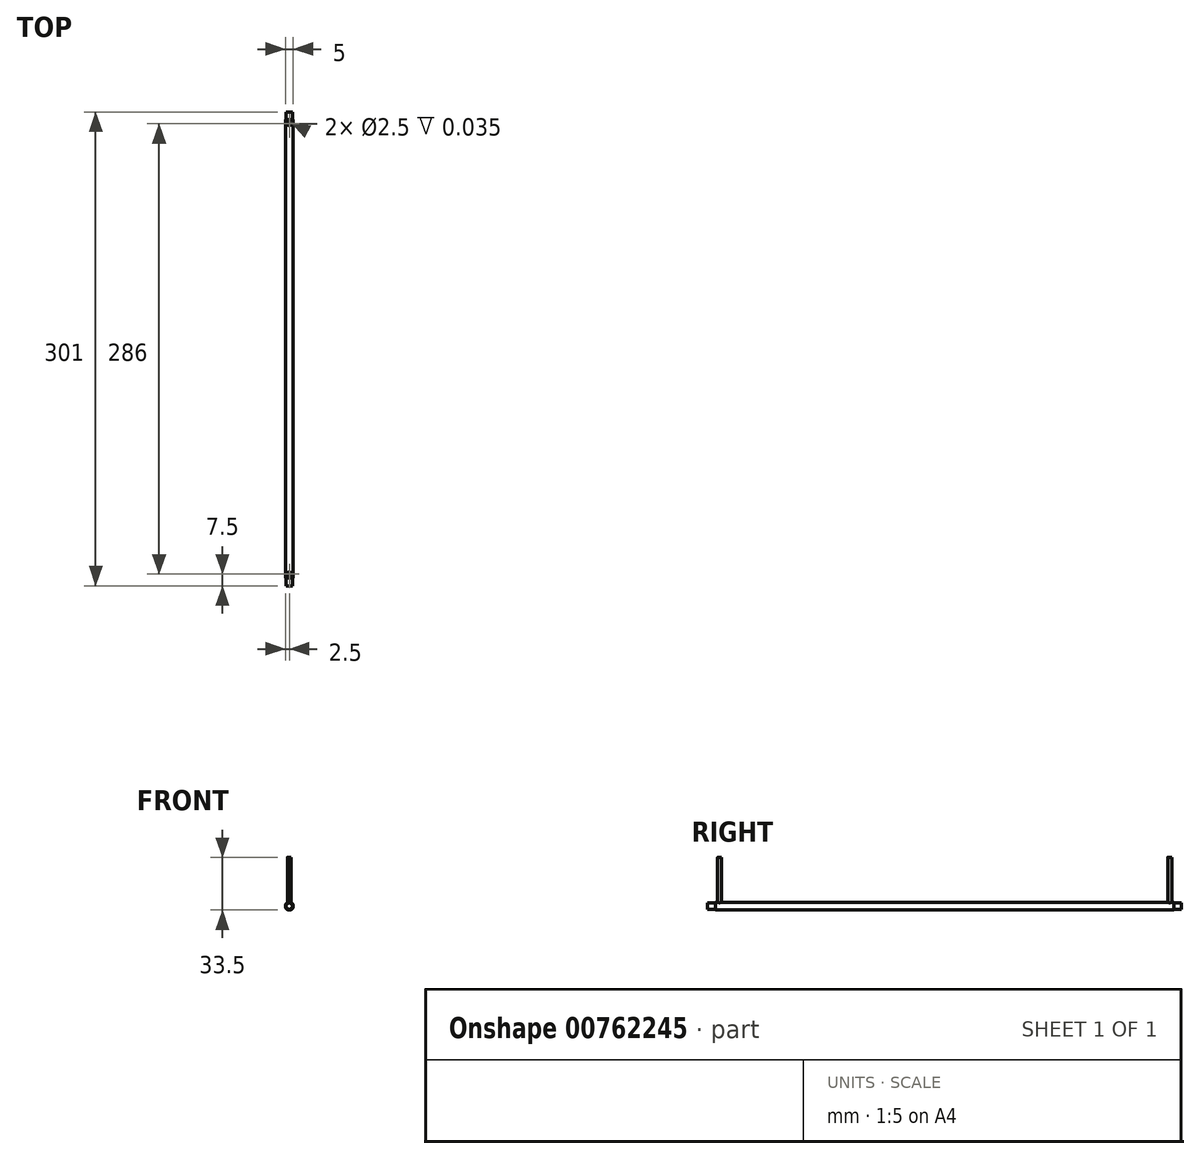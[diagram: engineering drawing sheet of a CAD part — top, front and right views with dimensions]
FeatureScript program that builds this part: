
annotation { "Feature Type Name" : "Feature", "Feature Type Description" : "" }
export const myFeature = defineFeature(function(context is Context, id is Id, definition is map)
    precondition{}
    {
        {
            var Q0;
            Q0=qCreatedBy(makeId("Front.planeOp"),FACE);
            var sketch = newSketch(context, id + "F0", { "sketchPlane" : qUnion([Q0])});
            skCircle(sketch, "E0", {"center": v(0, 0) * mm, "radius": 2.5 * mm});
            skSolve(sketch);
        }
        {
            var Q0;
            Q0=makeQuery(id+"F0.imprint","IMPRINT",FACE,{"disambiguationData":[TD([[makeQuery(id+"F0.imprint","IMPRINT",EDGE,{"derivedFrom":sQuery(id+"F0.wireOp",EDGE,"E0")}),1.0]])]});
            var Q1;
            Q1=sQuery(id+"F0.wireOp",EDGE,"E0");
            extrude(context, id + "F1", {"entities" : qUnion([Q0]), "surfaceEntities" : qUnion([Q1]), "endBound" : BoundingType.SYMMETRIC, "depth" : 291 * mm, "offsetDistance" : 25 * mm});
        }
        {
            var Q0;
            Q0=qCreatedBy(makeId("Top.planeOp"),FACE);
            cPlane(context, id + "F2", {"entities" : qUnion([Q0]), "cplaneType" : CPlaneType.OFFSET, "offset" : 3 * mm, "width" : 150 * mm, "height" : 150 * mm});
        }
        {
            var Q0;
            Q0=qCreatedBy(id+"F2.planeOp",FACE);
            var sketch = newSketch(context, id + "F3", { "sketchPlane" : qUnion([Q0])});
            skPoint(sketch, "E1", {"position": v(0, -143) * mm});
            skPoint(sketch, "E2", {"position": v(0, 143) * mm});
            skSolve(sketch);
        }
        {
            var Q0;
            Q0=sQuery(id+"F3.wireOp",VERTEX,"E1");
            var Q1;
            Q1=makeQuery(id+"F1.opExtrude","SWEPT_BODY",BODY,{"disambiguationData":[OSD([sQuery(id+"F0.wireOp",EDGE,"E0")])]});
            hole(context, id + "F4", {"style" : HoleStyle.SIMPLE, "endStyle" : HoleEndStyle.BLIND, "holeDiameter" : 2.5 * mm, "majorDiameter" : 5 * mm, "holeDepth" : 4.2 * mm, "isTappedThrough" : true, "tappedDepth" : 12 * mm, "tapClearance" : 3, "locations" : qUnion([Q0]), "scope" : qUnion([Q1])});
        }
        {
            var Q0;
            Q0=sQuery(id+"F3.wireOp",VERTEX,"E2");
            var Q1;
            Q1=makeQuery(id+"F1.opExtrude","SWEPT_BODY",BODY,{"disambiguationData":[OSD([sQuery(id+"F0.wireOp",EDGE,"E0")])]});
            hole(context, id + "F5", {"style" : HoleStyle.SIMPLE, "endStyle" : HoleEndStyle.BLIND, "holeDiameter" : 2.5 * mm, "majorDiameter" : 5 * mm, "holeDepth" : 4.2 * mm, "isTappedThrough" : true, "tappedDepth" : 12 * mm, "tapClearance" : 3, "locations" : qUnion([Q0]), "scope" : qUnion([Q1])});
        }
        {
            var Q0;
            Q0=qCreatedBy(makeId("Top.planeOp"),FACE);
            cPlane(context, id + "F6", {"entities" : qUnion([Q0]), "cplaneType" : CPlaneType.OFFSET, "offset" : 2 * mm, "oppositeDirection" : true, "width" : 150 * mm, "height" : 150 * mm});
        }
        {
            var Q0;
            Q0=qCreatedBy(id+"F6.planeOp",FACE);
            var sketch = newSketch(context, id + "F7", { "sketchPlane" : qUnion([Q0])});
            skCircle(sketch, "E3", {"center": v(0, 143) * mm, "radius": 1.25 * mm});
            skSolve(sketch);
        }
        {
            var Q0;
            Q0 = qSketchRegion(id + "F7", true);
            extrude(context, id + "F8", {"entities" : qUnion([Q0]), "operationType" : NewBodyOperationType.ADD, "depth" : 33 * mm, "offsetDistance" : 25 * mm});
        }
        {
            var Q0;
            Q0=qCreatedBy(id+"F6.planeOp",FACE);
            var sketch = newSketch(context, id + "F9", { "sketchPlane" : qUnion([Q0])});
            skCircle(sketch, "E4", {"center": v(0, -143) * mm, "radius": 1.25 * mm});
            skSolve(sketch);
        }
        {
            var Q0;
            Q0 = qSketchRegion(id + "F9", true);
            extrude(context, id + "F10", {"entities" : qUnion([Q0]), "operationType" : NewBodyOperationType.ADD, "depth" : 33 * mm, "offsetDistance" : 25 * mm});
        }
        {
            var Q0;
            Q0=makeQuery(id+"F1.opExtrude","CAP_FACE",FACE,{"disambiguationData":[OSD([sQuery(id+"F0.wireOp",EDGE,"E0")])],"isStart":false});
            var sketch = newSketch(context, id + "F11", { "sketchPlane" : qUnion([Q0])});
            skCircle(sketch, "E5", {"center": v(0, 0) * mm, "radius": 2 * mm});
            skSolve(sketch);
        }
        {
            var Q0;
            Q0 = qSketchRegion(id + "F11", true);
            extrude(context, id + "F12", {"entities" : qUnion([Q0]), "operationType" : NewBodyOperationType.ADD, "depth" : 5 * mm, "offsetDistance" : 25 * mm});
        }
        {
            var Q0;
            Q0=makeQuery(id+"F1.opExtrude","CAP_FACE",FACE,{"disambiguationData":[OSD([sQuery(id+"F0.wireOp",EDGE,"E0")])],"isStart":true});
            var sketch = newSketch(context, id + "F13", { "sketchPlane" : qUnion([Q0])});
            skCircle(sketch, "E6", {"center": v(0, 0) * mm, "radius": 2 * mm});
            skSolve(sketch);
        }
        {
            var Q0;
            Q0 = qSketchRegion(id + "F13", true);
            extrude(context, id + "F14", {"entities" : qUnion([Q0]), "operationType" : NewBodyOperationType.ADD, "depth" : 5 * mm, "offsetDistance" : 25 * mm});
        }
    });
